# Revit family: 753290001_Grif.Orinal Porcelana Blanco
name_source: partatom
category: Plumbing Fixtures
units: mm (PartAtom-declared; Revit-internal decimal feet)

## family parameters
Always vertical = Yes
Cut with Voids When Loaded = No
Host = Wall
OmniClass Number = 23.31.11.00
OmniClass Title = Faucets
Part Type = Normal
Room Calculation Point = No
Round Connector Dimension = Use Diameter
Shared = No

## types (1)
- Type 1
    Alto = 322 mm  [stored 1.05643 ft]
    Ancho = 146 mm  [stored 0.479003 ft]
    Capacidad de flujo máximo por norma = 3,6 L/min a 20 Ps
    Creado por = BIMBAU
    Cuidado Y Limpieza = Los acabados superficiales son aquellos que le imprimen una apariencia especial y estética a su producto y además le brindan protección. Para prolongar sus cualidades es vital que la limpieza profunda del producto se haga únicamente con agua y jabón suave y que en el secado y el brillo se utilice un paño de algodón limpio, dicha limpieza se recomienda 2 veces a la semana, y en zonas costeras a diario por la salinidad del ambiente. Por ningún motivo deben usarse elementos abrasivos, ácidos o disolventes para la limpieza del producto. Los acabados pueden variar su comportamiento en zonas costeras y/o en ambientes corrosivos.
    Default Elevation = 0 mm  [stored 0 ft]
    Description = Las válvulas para orinal Corona son el aliado perfecto para las necesidades de las instituciones de alto tráfico, 
están diseñadas para un óptimo funcionamiento y durabilidad debido a sus características antivandálicas
    Diámetro = 65.1 mm  [stored 0.213583 ft]
    Entrada minimo = 1/2P NPT.
    Fecha de creación = 13/04/2021
    Manufacturer = Corona
    Material = Corona_Cromado
    Material 2 = Corona_Porcelana_Sanitaria_Blanco
    Model = Grifería Orinal Porcelana Blanco
    Normatividad = NTC 920 y 1644
    Peso Bruto aprox = 440g 1,10lb.
    Peso Neto aprox = 390g 0,99lb.
    Presion maxima = 80 Psi.
    Presion minima = 10 Psi.
    Presión de agua = 10 - 80 Psi.
    Recubrimientos = -Resistente a la corrosión, pelado y decoloración por agua. -Recubrimientos no tóxicos.
    Referencia = 753290001
    Salida = Instalación por sistema de empaque de selle.
    Type Comments = -Grifiería para orinal de llave en porcelana / Cromada.
    URL = https://corona.co
    Vida útil = 150 Mil Ciclos.

note: [stored X ft] marks values corroborated as IEEE doubles in the binary element streams (Revit-internal decimal feet)

## geometry (parser evidence)
native form markers: Sweep x2
no freeform markers — native parametric forms only
